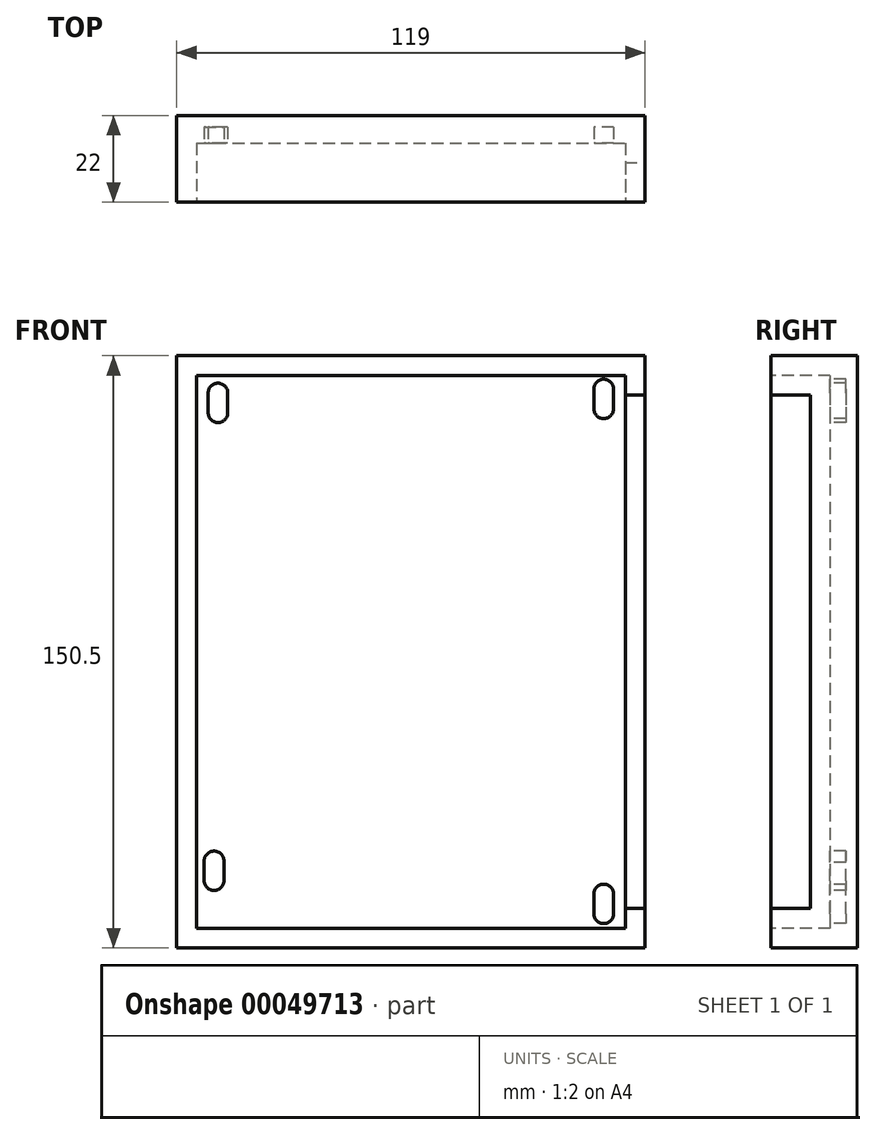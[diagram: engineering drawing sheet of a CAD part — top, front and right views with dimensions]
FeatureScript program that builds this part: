
annotation { "Feature Type Name" : "Feature", "Feature Type Description" : "" }
export const myFeature = defineFeature(function(context is Context, id is Id, definition is map)
    precondition{}
    {
        {
            var Q0;
            Q0=qCreatedBy(makeId("Front.planeOp"),FACE);
            var sketch = newSketch(context, id + "F0", { "sketchPlane" : qUnion([Q0])});
            skLineSegment(sketch, "E0.rect.bottom", {"start": v(-59.5, 75.25) * mm, "end": v(59.5, 75.25) * mm});
            skLineSegment(sketch, "E0.rect.top", {"start": v(-59.5, -75.25) * mm, "end": v(59.5, -75.25) * mm});
            skLineSegment(sketch, "E0.rect.left", {"start": v(-59.5, 75.25) * mm, "end": v(-59.5, -75.25) * mm});
            skLineSegment(sketch, "E0.rect.right", {"start": v(59.5, 75.25) * mm, "end": v(59.5, -75.25) * mm});
            skPoint(sketch, "E0.rect.middle", {"position": v(0, 0) * mm});
            skSolve(sketch);
        }
        {
            var Q0;
            Q0 = qSketchRegion(id + "F0", true);
            extrude(context, id + "F1", {"entities" : qUnion([Q0]), "depth" : 22 * mm});
        }
        {
            var Q0;
            Q0=makeQuery(id+"F1.opExtrude","CAP_FACE",FACE,{"disambiguationData":[OSD([sQuery(id+"F0.wireOp",EDGE,"E0.rect.bottom"),sQuery(id+"F0.wireOp",EDGE,"E0.rect.top"),sQuery(id+"F0.wireOp",EDGE,"E0.rect.left"),sQuery(id+"F0.wireOp",EDGE,"E0.rect.right")])],"isStart":false});
            var sketch = newSketch(context, id + "F2", { "sketchPlane" : qUnion([Q0])});
            skLineSegment(sketch, "E1.rect.bottom", {"start": v(-54.5, 70.25) * mm, "end": v(54.5, 70.25) * mm});
            skLineSegment(sketch, "E1.rect.top", {"start": v(-54.5, -70.25) * mm, "end": v(54.5, -70.25) * mm});
            skLineSegment(sketch, "E1.rect.left", {"start": v(-54.5, 70.25) * mm, "end": v(-54.5, -70.25) * mm});
            skLineSegment(sketch, "E1.rect.right", {"start": v(54.5, 70.25) * mm, "end": v(54.5, -70.25) * mm});
            skPoint(sketch, "E1.rect.middle", {"position": v(0, 0) * mm});
            skSolve(sketch);
        }
        {
            var Q0;
            Q0=makeQuery(id+"F2.imprint","IMPRINT",FACE,{"disambiguationData":[TD([[makeQuery(id+"F2.imprint","IMPRINT",EDGE,{"derivedFrom":sQuery(id+"F2.wireOp",EDGE,"E1.rect.bottom")}),-1.0]])]});
            extrude(context, id + "F3", {"entities" : qUnion([Q0]), "operationType" : NewBodyOperationType.REMOVE, "oppositeDirection" : true, "depth" : 15 * mm});
        }
        {
            var Q0;
            Q0=makeQuery(id+"F1.opExtrude","SWEPT_FACE",FACE,{"disambiguationData":[OSD([sQuery(id+"F0.wireOp",EDGE,"E0.rect.right")])]});
            var sketch = newSketch(context, id + "F4", { "sketchPlane" : qUnion([Q0])});
            skLineSegment(sketch, "E2", {"start": v(-22, 0) * mm, "end": v(-22, -65.25) * mm});
            skLineSegment(sketch, "E3", {"start": v(-22, -65.25) * mm, "end": v(-12, -65.25) * mm});
            skLineSegment(sketch, "E4", {"start": v(-12, -65.25) * mm, "end": v(-12, 0) * mm});
            skLineSegment(sketch, "E5", {"start": v(-12, 0) * mm, "end": v(-12, 65.25) * mm});
            skLineSegment(sketch, "E6", {"start": v(-12, 65.25) * mm, "end": v(-22, 65.25) * mm});
            skLineSegment(sketch, "E7", {"start": v(-22, 65.25) * mm, "end": v(-22, 0) * mm});
            skSolve(sketch);
        }
        {
            var Q0;
            Q0=makeQuery(id+"F4.imprint","IMPRINT",FACE,{"disambiguationData":[TD([[makeQuery(id+"F4.imprint","IMPRINT",EDGE,{"derivedFrom":sQuery(id+"F4.wireOp",EDGE,"E2")}),1.0]])]});
            extrude(context, id + "F5", {"entities" : qUnion([Q0]), "operationType" : NewBodyOperationType.REMOVE, "oppositeDirection" : true, "depth" : 25 * mm});
        }
        {
            var Q0;
            Q0=makeQuery(id+"F3.boolean.opBoolean","COPY",FACE,{"derivedFrom":makeQuery(id+"F3.opExtrude","CAP_FACE",FACE,{"disambiguationData":[OSD([sQuery(id+"F2.wireOp",EDGE,"E1.rect.bottom"),sQuery(id+"F2.wireOp",EDGE,"E1.rect.top"),sQuery(id+"F2.wireOp",EDGE,"E1.rect.left"),sQuery(id+"F2.wireOp",EDGE,"E1.rect.right")])],"isStart":false})});
            var sketch = newSketch(context, id + "F6", { "sketchPlane" : qUnion([Q0])});
            skLineSegment(sketch, "E8", {"start": v(-54.5, 65.75) * mm, "end": v(-49, 65.75) * mm, "construction": true});
            skLineSegment(sketch, "E9", {"start": v(-49, 65.75) * mm, "end": v(-49, 70.25) * mm, "construction": true});
            skLineSegment(sketch, "E10", {"start": v(54.5, 66.75) * mm, "end": v(49, 66.75) * mm, "construction": true});
            skLineSegment(sketch, "E11", {"start": v(49, 66.75) * mm, "end": v(49, 70.25) * mm, "construction": true});
            skLineSegment(sketch, "E12", {"start": v(49, -70.25) * mm, "end": v(49, -66.55) * mm, "construction": true});
            skLineSegment(sketch, "E13", {"start": v(49, -66.55) * mm, "end": v(54.5, -66.55) * mm, "construction": true});
            skLineSegment(sketch, "E14", {"start": v(-54.5, -58.15) * mm, "end": v(-50, -58.15) * mm, "construction": true});
            skLineSegment(sketch, "E15", {"start": v(-50, -58.15) * mm, "end": v(-50, -70.25) * mm, "construction": true});
            skArc(sketch, "E16", {"start": v(-46.5, 65.75) * mm, "mid": v(-49, 68.25) * mm, "end": v(-51.5, 65.75) * mm});
            skArc(sketch, "E17", {"start": v(51.5, 66.75) * mm, "mid": v(49, 69.25) * mm, "end": v(46.5, 66.75) * mm});
            skArc(sketch, "E18", {"start": v(46.5, -66.55) * mm, "mid": v(49, -69.05) * mm, "end": v(51.5, -66.55) * mm});
            skArc(sketch, "E19", {"start": v(-52.5, -58.15) * mm, "mid": v(-50, -60.65) * mm, "end": v(-47.5, -58.15) * mm});
            skPoint(sketch, "E20.startSnap0", {"position": v(-52.25, -58.15) * mm});
            skLineSegment(sketch, "E21", {"start": v(-51.5, 65.75) * mm, "end": v(-51.5, 60.75) * mm});
            skPoint(sketch, "E21.startSnap0", {"position": v(-51.75, 65.75) * mm});
            skLineSegment(sketch, "E22", {"start": v(-46.5, 65.75) * mm, "end": v(-46.5, 60.75) * mm});
            skLineSegment(sketch, "E23", {"start": v(46.5, 66.75) * mm, "end": v(46.5, 61.75) * mm});
            skLineSegment(sketch, "E24", {"start": v(51.5, 66.75) * mm, "end": v(51.5, 61.75) * mm});
            skLineSegment(sketch, "E25", {"start": v(46.5, -66.55) * mm, "end": v(46.5, -61.55) * mm});
            skLineSegment(sketch, "E26", {"start": v(51.5, -66.55) * mm, "end": v(51.5, -61.55) * mm});
            skLineSegment(sketch, "E27", {"start": v(-47.5, -58.52) * mm, "end": v(-47.5, -53.52) * mm});
            skLineSegment(sketch, "E28", {"start": v(-52.5, -58.15) * mm, "end": v(-52.5, -53.15) * mm});
            skArc(sketch, "E29", {"start": v(-51.5, 60.75) * mm, "mid": v(-49, 58.25) * mm, "end": v(-46.5, 60.75) * mm});
            skArc(sketch, "E30", {"start": v(46.5, 61.75) * mm, "mid": v(49, 59.25) * mm, "end": v(51.5, 61.75) * mm});
            skArc(sketch, "E31", {"start": v(51.5, -61.55) * mm, "mid": v(49, -59.05) * mm, "end": v(46.5, -61.55) * mm});
            skArc(sketch, "E32", {"start": v(-47.5, -53.52) * mm, "mid": v(-49.8, -50.64) * mm, "end": v(-52.5, -53.15) * mm});
            skSolve(sketch);
        }
        {
            var Q0;
            Q0=makeQuery(id+"F6.imprint","IMPRINT",FACE,{"disambiguationData":[TD([[makeQuery(id+"F6.imprint","IMPRINT",EDGE,{"derivedFrom":sQuery(id+"F6.wireOp",EDGE,"E16")}),1.0]])]});
            var Q1;
            Q1=makeQuery(id+"F6.imprint","IMPRINT",FACE,{"disambiguationData":[TD([[makeQuery(id+"F6.imprint","IMPRINT",EDGE,{"derivedFrom":sQuery(id+"F6.wireOp",EDGE,"E17")}),1.0]])]});
            var Q2;
            Q2=makeQuery(id+"F6.imprint","IMPRINT",FACE,{"disambiguationData":[TD([[makeQuery(id+"F6.imprint","IMPRINT",EDGE,{"derivedFrom":sQuery(id+"F6.wireOp",EDGE,"E18")}),1.0]])]});
            var Q3;
            {var subQ2=sQuery(id+"F6.wireOp",EDGE,"E19");Q3=makeQuery(id+"F6.imprint","IMPRINT",FACE,{"disambiguationData":[TD([[makeQuery(id+"F6.imprint","IMPRINT",EDGE,{"derivedFrom":subQ2}),1.0]])]});}
            extrude(context, id + "F7", {"entities" : qUnion([Q0, Q1, Q2, Q3]), "operationType" : NewBodyOperationType.REMOVE, "oppositeDirection" : true, "depth" : 4 * mm});
        }
    });
